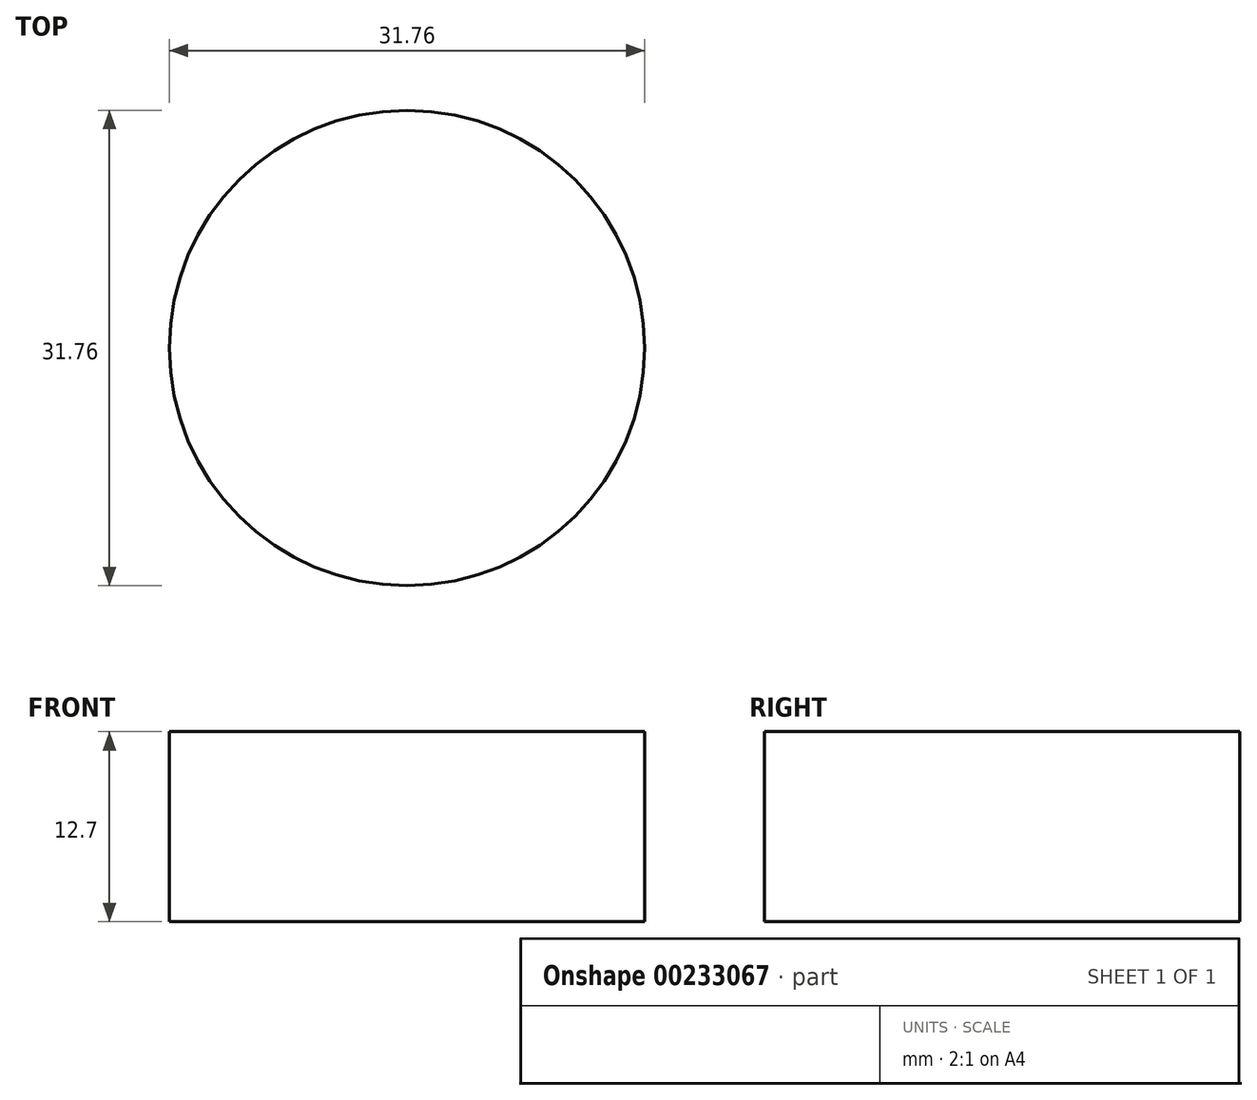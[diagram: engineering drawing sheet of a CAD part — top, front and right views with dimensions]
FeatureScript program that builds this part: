
annotation { "Feature Type Name" : "Feature", "Feature Type Description" : "" }
export const myFeature = defineFeature(function(context is Context, id is Id, definition is map)
    precondition{}
    {
        {
            var Q0;
            Q0=qCreatedBy(makeId("Top.planeOp"),FACE);
            var sketch = newSketch(context, id + "F0", { "sketchPlane" : qUnion([Q0])});
            skCircle(sketch, "E0", {"center": v(0, 0) * mm, "radius": 15.88 * mm});
            skSolve(sketch);
        }
        {
            var Q0;
            Q0=makeQuery(id+"F0.imprint","IMPRINT",FACE,{"disambiguationData":[TD([[makeQuery(id+"F0.imprint","IMPRINT",EDGE,{"derivedFrom":sQuery(id+"F0.wireOp",EDGE,"E0")}),1.0]])]});
            extrude(context, id + "F1", {"entities" : qUnion([Q0]), "depth" : 12.7 * mm});
        }
    });
